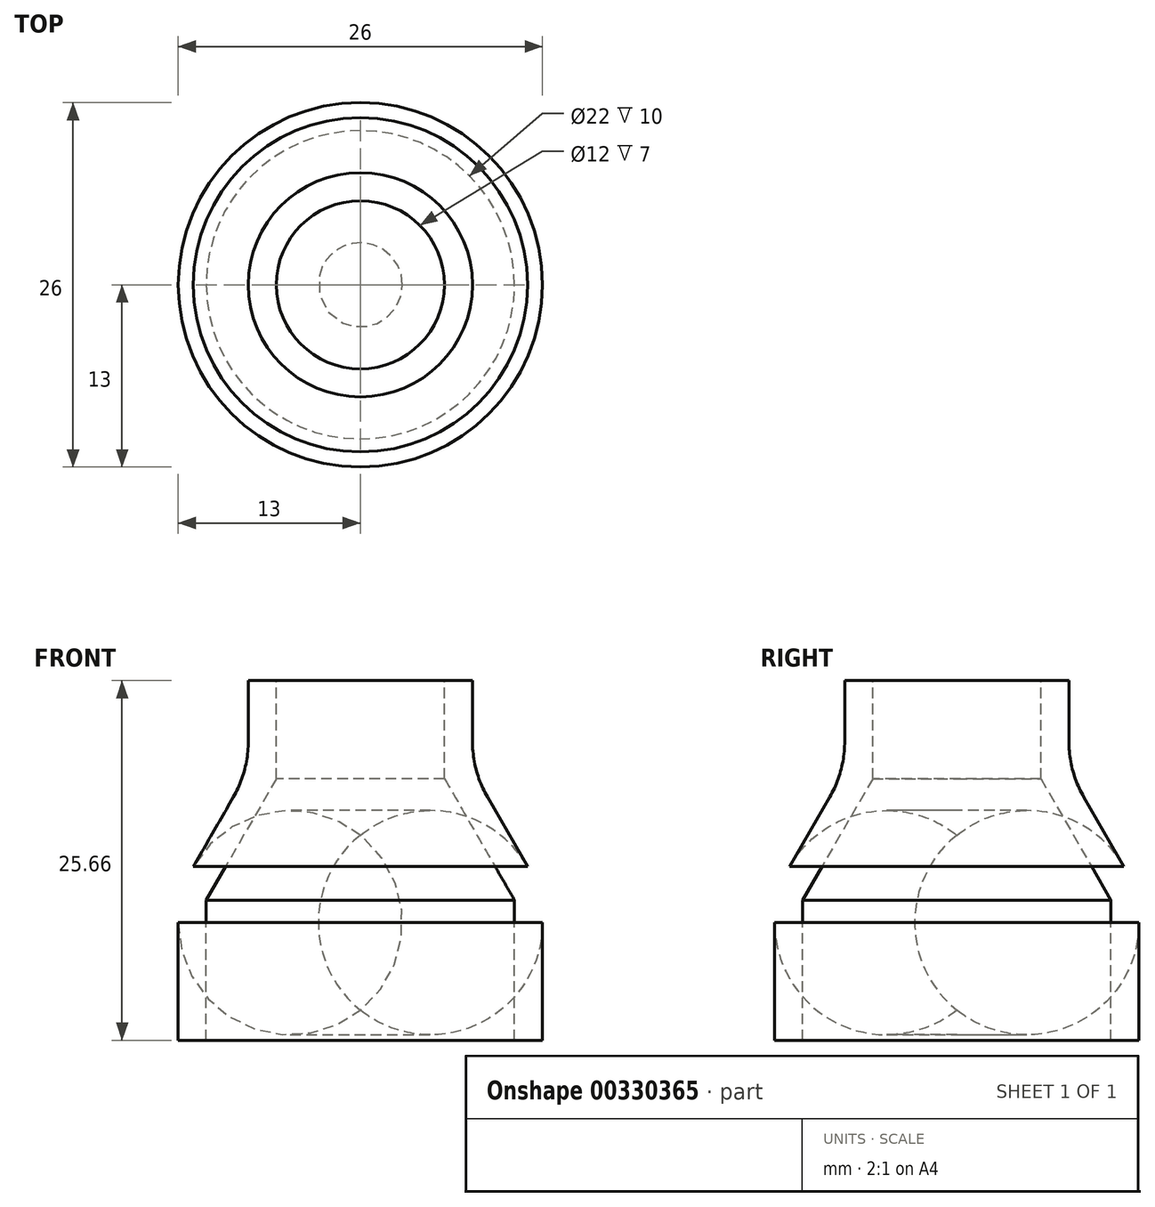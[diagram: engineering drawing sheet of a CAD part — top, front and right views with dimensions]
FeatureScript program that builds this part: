
annotation { "Feature Type Name" : "Feature", "Feature Type Description" : "" }
export const myFeature = defineFeature(function(context is Context, id is Id, definition is map)
    precondition{}
    {
        {
            var Q0;
            Q0=qCreatedBy(makeId("Front.planeOp"),FACE);
            var sketch = newSketch(context, id + "F0", { "sketchPlane" : qUnion([Q0])});
            skLineSegment(sketch, "E0", {"start": v(-11, 0) * mm, "end": v(-11, 10) * mm});
            skLineSegment(sketch, "E1", {"start": v(-11, 10) * mm, "end": v(-6, 18.66) * mm});
            skLineSegment(sketch, "E2", {"start": v(-6, 18.66) * mm, "end": v(-6, 25.66) * mm});
            skLineSegment(sketch, "E3.0", {"start": v(-8, 19.2) * mm, "end": v(-8, 25.66) * mm});
            skLineSegment(sketch, "E3.1", {"start": v(-13, 10.54) * mm, "end": v(-8, 19.2) * mm});
            skLineSegment(sketch, "E3.2", {"start": v(-13, 0) * mm, "end": v(-13, 10.54) * mm});
            skLineSegment(sketch, "E4", {"start": v(-8, 25.66) * mm, "end": v(-6, 25.66) * mm});
            skLineSegment(sketch, "E5", {"start": v(-13, 0) * mm, "end": v(-11, 0) * mm});
            skLineSegment(sketch, "E6", {"start": v(0, 41.45) * mm, "end": v(0, 0) * mm, "construction": true});
            skSolve(sketch);
        }
        {
            var Q0;
            Q0=makeQuery(id+"F0.imprint","IMPRINT",FACE,{"disambiguationData":[TD([[makeQuery(id+"F0.imprint","IMPRINT",EDGE,{"derivedFrom":sQuery(id+"F0.wireOp",EDGE,"E0")}),1.0]])]});
            var Q1;
            Q1=sQuery(id+"F0.wireOp",EDGE,"E6");
            revolve(context, id + "F1", {"entities" : qUnion([Q0]), "axis" : qUnion([Q1]), "revolveType" : RevolveType.FULL});
        }
        {
            var Q0;
            Q0=makeQuery(id+"F1.opRevolve","SWEPT_EDGE",EDGE,{"disambiguationData":[OSD([sQuery(id+"F0.wireOp",EDGE,"E3.1"),sQuery(id+"F0.wireOp",EDGE,"E3.2")])]});
            var Q1;
            Q1=makeQuery(id+"F1.opRevolve","SWEPT_EDGE",EDGE,{"disambiguationData":[OSD([sQuery(id+"F0.wireOp",EDGE,"E3.0"),sQuery(id+"F0.wireOp",EDGE,"E3.1")])]});
            fillet(context, id + "F2", {"entities" : qUnion([Q0, Q1]), "radius" : 8 * mm, "tangentPropagation" : true, "allowEdgeOverflow" : false});
        }
    });
